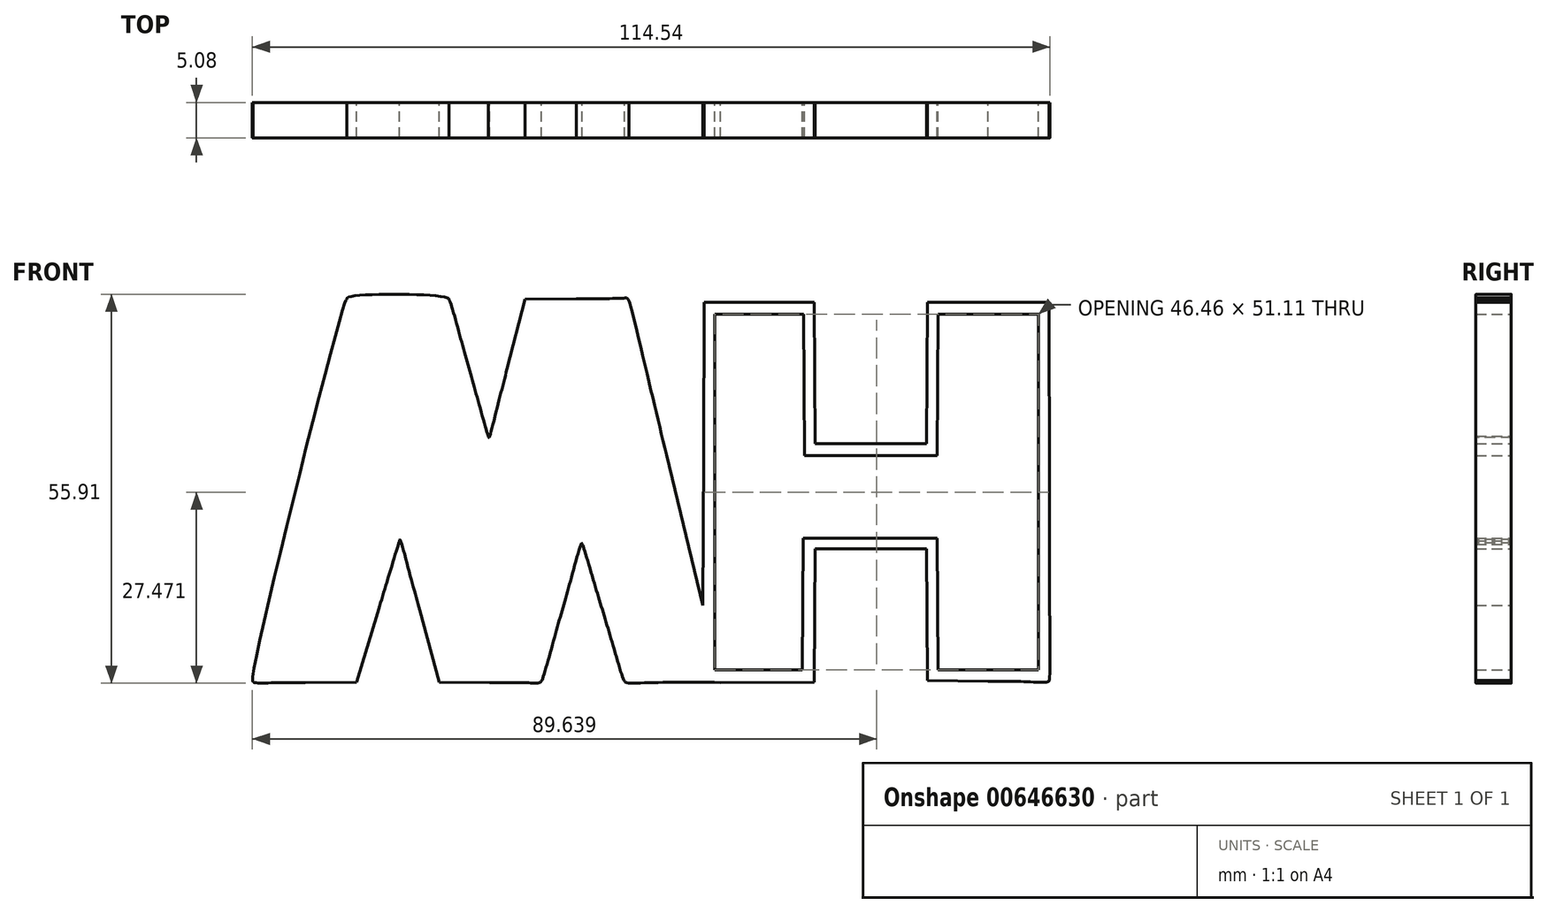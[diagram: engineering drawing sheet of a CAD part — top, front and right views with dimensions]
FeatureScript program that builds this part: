
annotation { "Feature Type Name" : "Feature", "Feature Type Description" : "" }
export const myFeature = defineFeature(function(context is Context, id is Id, definition is map)
    precondition{}
    {
        {
            var Q0;
            Q0=qCreatedBy(makeId("Front.planeOp"),FACE);
            var sketch = newSketch(context, id + "F0", { "sketchPlane" : qUnion([Q0])});
            skFitSpline(sketch, "E0", {"points": [v(-88.7, -151.63) * mm, v(-88.8, -151.45) * mm, v(-75.5, -97.15) * mm, v(-75.25, -96.73) * mm]});
            skFitSpline(sketch, "E1", {"points": [v(-75.25, -96.73) * mm, v(-75.03, -96.37) * mm, v(-60.84, -96.44) * mm, v(-60.58, -96.8) * mm]});
            skFitSpline(sketch, "E2", {"points": [v(-60.58, -96.8) * mm, v(-60.45, -96.96) * mm, v(-59.17, -101.33) * mm, v(-57.72, -106.5) * mm]});
            skFitSpline(sketch, "E3", {"points": [v(-57.72, -106.5) * mm, v(-56.28, -111.68) * mm, v(-55.03, -116.1) * mm, v(-54.95, -116.32) * mm]});
            skFitSpline(sketch, "E4", {"points": [v(-54.95, -116.32) * mm, v(-54.86, -116.55) * mm, v(-53.7, -112.42) * mm, v(-52.23, -106.68) * mm]});
            skFitSpline(sketch, "E5", {"points": [v(-42.31, -96.57) * mm, v(-35.5, -96.5) * mm, v(-34.95, -96.53) * mm, v(-34.76, -96.91) * mm]});
            skFitSpline(sketch, "E6", {"points": [v(-34.76, -96.91) * mm, v(-34.64, -97.14) * mm, v(-32.2, -107.08) * mm, v(-29.35, -119) * mm]});
            skLineSegment(sketch, "E7", {"start": v(-52.23, -106.68) * mm, "end": v(-49.66, -96.63) * mm});
            skLineSegment(sketch, "E8", {"start": v(-49.66, -96.63) * mm, "end": v(-42.31, -96.57) * mm});
            skFitSpline(sketch, "E9", {"points": [v(25.63, -124.16) * mm, v(25.66, -139.04) * mm, v(25.65, -151.33) * mm, v(25.6, -151.45) * mm]});
            skFitSpline(sketch, "E10", {"points": [v(25.6, -151.45) * mm, v(25.54, -151.6) * mm, v(22.51, -151.65) * mm, v(16.83, -151.57) * mm]});
            skLineSegment(sketch, "E11", {"start": v(-29.35, -119) * mm, "end": v(-24.15, -140.68) * mm});
            skLineSegment(sketch, "E12", {"start": v(-24.15, -140.68) * mm, "end": v(-24.03, -118.89) * mm});
            skLineSegment(sketch, "E13", {"start": v(-24.03, -118.89) * mm, "end": v(-23.91, -97.1) * mm});
            skLineSegment(sketch, "E14", {"start": v(-23.91, -97.1) * mm, "end": v(-16.01, -97.1) * mm});
            skLineSegment(sketch, "E15", {"start": v(-16.01, -97.1) * mm, "end": v(-8.12, -97.1) * mm});
            skLineSegment(sketch, "E16", {"start": v(-8.12, -97.1) * mm, "end": v(-8.06, -107.26) * mm});
            skLineSegment(sketch, "E17", {"start": v(-8.06, -107.26) * mm, "end": v(-8, -117.42) * mm});
            skLineSegment(sketch, "E18", {"start": v(-8, -117.42) * mm, "end": v(0.02, -117.42) * mm});
            skLineSegment(sketch, "E19", {"start": v(0.02, -117.42) * mm, "end": v(8.03, -117.42) * mm});
            skLineSegment(sketch, "E20", {"start": v(8.03, -117.42) * mm, "end": v(8.09, -107.26) * mm});
            skLineSegment(sketch, "E21", {"start": v(8.09, -107.26) * mm, "end": v(8.15, -97.1) * mm});
            skLineSegment(sketch, "E22", {"start": v(8.15, -97.1) * mm, "end": v(16.86, -97.1) * mm});
            skLineSegment(sketch, "E23", {"start": v(16.86, -97.1) * mm, "end": v(25.57, -97.1) * mm});
            skLineSegment(sketch, "E24", {"start": v(25.57, -97.1) * mm, "end": v(25.63, -124.16) * mm});
            skFitSpline(sketch, "E25", {"points": [v(-21.62, -151.75) * mm, v(-32.25, -151.8) * mm, v(-35.17, -151.74) * mm, v(-35.35, -151.51) * mm]});
            skFitSpline(sketch, "E26", {"points": [v(-35.35, -151.51) * mm, v(-35.48, -151.35) * mm, v(-36.87, -146.94) * mm, v(-38.44, -141.7) * mm]});
            skFitSpline(sketch, "E27", {"points": [v(-38.44, -141.7) * mm, v(-40, -136.46) * mm, v(-41.35, -132.04) * mm, v(-41.43, -131.89) * mm]});
            skFitSpline(sketch, "E28", {"points": [v(-41.43, -131.89) * mm, v(-41.52, -131.73) * mm, v(-42.82, -136.02) * mm, v(-44.34, -141.41) * mm]});
            skFitSpline(sketch, "E29", {"points": [v(-44.34, -141.41) * mm, v(-45.86, -146.8) * mm, v(-47.2, -151.35) * mm, v(-47.33, -151.52) * mm]});
            skFitSpline(sketch, "E30", {"points": [v(-47.33, -151.52) * mm, v(-47.5, -151.74) * mm, v(-49.17, -151.8) * mm, v(-54.76, -151.75) * mm]});
            skLineSegment(sketch, "E31", {"start": v(16.83, -151.57) * mm, "end": v(8.15, -151.45) * mm});
            skLineSegment(sketch, "E32", {"start": v(8.15, -151.45) * mm, "end": v(8.09, -141.99) * mm});
            skLineSegment(sketch, "E33", {"start": v(8.09, -141.99) * mm, "end": v(8.03, -132.52) * mm});
            skLineSegment(sketch, "E34", {"start": v(8.03, -132.52) * mm, "end": v(0.02, -132.52) * mm});
            skLineSegment(sketch, "E35", {"start": v(0.02, -132.52) * mm, "end": v(-8, -132.52) * mm});
            skLineSegment(sketch, "E36", {"start": v(-8, -132.52) * mm, "end": v(-8.06, -142.1) * mm});
            skLineSegment(sketch, "E37", {"start": v(-8.06, -142.1) * mm, "end": v(-8.12, -151.69) * mm});
            skLineSegment(sketch, "E38", {"start": v(-8.12, -151.69) * mm, "end": v(-21.62, -151.75) * mm});
            skFitSpline(sketch, "E39", {"points": [v(-64.77, -141.38) * mm, v(-66.31, -135.72) * mm, v(-67.62, -131.22) * mm, v(-67.68, -131.4) * mm]});
            skFitSpline(sketch, "E40", {"points": [v(-67.68, -131.4) * mm, v(-67.74, -131.57) * mm, v(-69.16, -136.2) * mm, v(-70.83, -141.7) * mm]});
            skLineSegment(sketch, "E41", {"start": v(-54.76, -151.75) * mm, "end": v(-61.97, -151.69) * mm});
            skLineSegment(sketch, "E42", {"start": v(-61.97, -151.69) * mm, "end": v(-64.77, -141.38) * mm});
            skFitSpline(sketch, "E43", {"points": [v(-81.23, -151.75) * mm, v(-85.27, -151.78) * mm, v(-88.64, -151.73) * mm, v(-88.7, -151.63) * mm]});
            skLineSegment(sketch, "E44", {"start": v(-70.83, -141.7) * mm, "end": v(-73.87, -151.69) * mm});
            skLineSegment(sketch, "E45", {"start": v(-73.87, -151.69) * mm, "end": v(-81.23, -151.75) * mm});
            skFitSpline(sketch, "E46", {"points": [v(-71.54, -137.8) * mm, v(-69.52, -131.13) * mm, v(-67.82, -125.58) * mm, v(-67.76, -125.47) * mm]});
            skFitSpline(sketch, "E47", {"points": [v(-67.76, -125.47) * mm, v(-67.7, -125.37) * mm, v(-67.54, -125.4) * mm, v(-67.4, -125.53) * mm]});
            skFitSpline(sketch, "E48", {"points": [v(-67.4, -125.53) * mm, v(-67.26, -125.67) * mm, v(-65.67, -131.2) * mm, v(-63.87, -137.8) * mm]});
            skFitSpline(sketch, "E49", {"points": [v(-45.2, -137.75) * mm, v(-43.32, -131.1) * mm, v(-41.7, -125.67) * mm, v(-41.58, -125.67) * mm]});
            skFitSpline(sketch, "E50", {"points": [v(-41.58, -125.67) * mm, v(-41.47, -125.67) * mm, v(-39.74, -131.1) * mm, v(-37.74, -137.75) * mm]});
            skLineSegment(sketch, "E51", {"start": v(-63.87, -137.8) * mm, "end": v(-60.59, -149.83) * mm});
            skLineSegment(sketch, "E52", {"start": v(-60.59, -149.83) * mm, "end": v(-54.6, -149.83) * mm});
            skLineSegment(sketch, "E53", {"start": v(-54.6, -149.83) * mm, "end": v(-48.6, -149.83) * mm});
            skLineSegment(sketch, "E54", {"start": v(-48.6, -149.83) * mm, "end": v(-45.2, -137.75) * mm});
            skFitSpline(sketch, "E55", {"points": [v(-24.16, -148.85) * mm, v(-24.25, -148.24) * mm, v(-26.82, -137.34) * mm, v(-29.88, -124.62) * mm]});
            skFitSpline(sketch, "E56", {"points": [v(-29.88, -124.62) * mm, v(-32.93, -111.9) * mm, v(-35.6, -100.8) * mm, v(-35.8, -99.93) * mm]});
            skLineSegment(sketch, "E57", {"start": v(-37.74, -137.75) * mm, "end": v(-34.1, -149.83) * mm});
            skLineSegment(sketch, "E58", {"start": v(-34.1, -149.83) * mm, "end": v(-29.05, -149.9) * mm});
            skLineSegment(sketch, "E59", {"start": v(-29.05, -149.9) * mm, "end": v(-24, -149.95) * mm});
            skLineSegment(sketch, "E60", {"start": v(-24, -149.95) * mm, "end": v(-24.16, -148.85) * mm});
            skFitSpline(sketch, "E61", {"points": [v(-51.35, -110.54) * mm, v(-53.05, -117.17) * mm, v(-54.55, -122.7) * mm, v(-54.68, -122.84) * mm]});
            skFitSpline(sketch, "E62", {"points": [v(-54.68, -122.84) * mm, v(-54.98, -123.14) * mm, v(-54.64, -124.25) * mm, v(-58.3, -111.15) * mm]});
            skFitSpline(sketch, "E63", {"points": [v(-58.3, -111.15) * mm, v(-60.04, -104.95) * mm, v(-61.56, -99.54) * mm, v(-61.7, -99.12) * mm]});
            skLineSegment(sketch, "E64", {"start": v(-35.8, -99.93) * mm, "end": v(-36.15, -98.36) * mm});
            skLineSegment(sketch, "E65", {"start": v(-36.15, -98.36) * mm, "end": v(-42.2, -98.42) * mm});
            skLineSegment(sketch, "E66", {"start": v(-42.2, -98.42) * mm, "end": v(-48.27, -98.49) * mm});
            skLineSegment(sketch, "E67", {"start": v(-48.27, -98.49) * mm, "end": v(-51.35, -110.54) * mm});
            skFitSpline(sketch, "E68", {"points": [v(-80.12, -123.75) * mm, v(-83.56, -137.71) * mm, v(-86.42, -149.31) * mm, v(-86.47, -149.54) * mm]});
            skFitSpline(sketch, "E69", {"points": [v(-86.47, -149.54) * mm, v(-86.57, -149.92) * mm, v(-86.2, -149.94) * mm, v(-80.9, -149.94) * mm]});
            skLineSegment(sketch, "E70", {"start": v(-61.7, -99.12) * mm, "end": v(-61.93, -98.37) * mm});
            skLineSegment(sketch, "E71", {"start": v(-61.93, -98.37) * mm, "end": v(-67.9, -98.37) * mm});
            skLineSegment(sketch, "E72", {"start": v(-67.9, -98.37) * mm, "end": v(-73.88, -98.37) * mm});
            skLineSegment(sketch, "E73", {"start": v(-73.88, -98.37) * mm, "end": v(-80.12, -123.75) * mm});
            skLineSegment(sketch, "E74", {"start": v(-80.9, -149.94) * mm, "end": v(-75.22, -149.94) * mm});
            skLineSegment(sketch, "E75", {"start": v(-75.22, -149.94) * mm, "end": v(-71.54, -137.8) * mm});
            skLineSegment(sketch, "E76", {"start": v(-9.8, -140.48) * mm, "end": v(-9.74, -131.01) * mm});
            skLineSegment(sketch, "E77", {"start": v(-9.74, -131.01) * mm, "end": v(-0.1, -131.01) * mm});
            skLineSegment(sketch, "E78", {"start": v(-0.1, -131.01) * mm, "end": v(9.54, -131.01) * mm});
            skLineSegment(sketch, "E79", {"start": v(9.54, -131.01) * mm, "end": v(9.6, -140.48) * mm});
            skLineSegment(sketch, "E80", {"start": v(9.6, -140.48) * mm, "end": v(9.66, -149.94) * mm});
            skLineSegment(sketch, "E81", {"start": v(9.66, -149.94) * mm, "end": v(16.86, -149.94) * mm});
            skLineSegment(sketch, "E82", {"start": v(16.86, -149.94) * mm, "end": v(24.06, -149.94) * mm});
            skLineSegment(sketch, "E83", {"start": v(24.06, -149.94) * mm, "end": v(24.06, -124.39) * mm});
            skLineSegment(sketch, "E84", {"start": v(24.06, -124.39) * mm, "end": v(24.06, -98.83) * mm});
            skLineSegment(sketch, "E85", {"start": v(24.06, -98.83) * mm, "end": v(16.86, -98.83) * mm});
            skLineSegment(sketch, "E86", {"start": v(16.86, -98.83) * mm, "end": v(9.66, -98.83) * mm});
            skLineSegment(sketch, "E87", {"start": v(9.66, -98.83) * mm, "end": v(9.6, -109) * mm});
            skLineSegment(sketch, "E88", {"start": v(9.6, -109) * mm, "end": v(9.54, -119.16) * mm});
            skLineSegment(sketch, "E89", {"start": v(9.54, -119.16) * mm, "end": v(0.02, -119.16) * mm});
            skLineSegment(sketch, "E90", {"start": v(0.02, -119.16) * mm, "end": v(-9.5, -119.16) * mm});
            skLineSegment(sketch, "E91", {"start": v(-9.5, -119.16) * mm, "end": v(-9.57, -109) * mm});
            skLineSegment(sketch, "E92", {"start": v(-9.57, -109) * mm, "end": v(-9.63, -98.83) * mm});
            skLineSegment(sketch, "E93", {"start": v(-9.63, -98.83) * mm, "end": v(-16.02, -98.83) * mm});
            skLineSegment(sketch, "E94", {"start": v(-16.02, -98.83) * mm, "end": v(-22.4, -98.83) * mm});
            skLineSegment(sketch, "E95", {"start": v(-22.4, -98.83) * mm, "end": v(-22.4, -124.39) * mm});
            skLineSegment(sketch, "E96", {"start": v(-22.4, -124.39) * mm, "end": v(-22.4, -149.94) * mm});
            skLineSegment(sketch, "E97", {"start": v(-22.4, -149.94) * mm, "end": v(-16.13, -149.94) * mm});
            skLineSegment(sketch, "E98", {"start": v(-16.13, -149.94) * mm, "end": v(-9.86, -149.94) * mm});
            skLineSegment(sketch, "E99", {"start": v(-9.86, -149.94) * mm, "end": v(-9.8, -140.48) * mm});
            skSolve(sketch);
        }
        {
            var Q0;
            Q0=makeQuery(id+"F0.imprint","IMPRINT",FACE,{"disambiguationData":[TD([[makeQuery(id+"F0.imprint","IMPRINT",EDGE,{"derivedFrom":sQuery(id+"F0.wireOp",EDGE,"E0")}),-1.0]])]});
            extrude(context, id + "F1", {"entities" : qUnion([Q0]), "depth" : 5.08 * mm, "offsetDistance" : 25.4 * mm});
        }
    });
